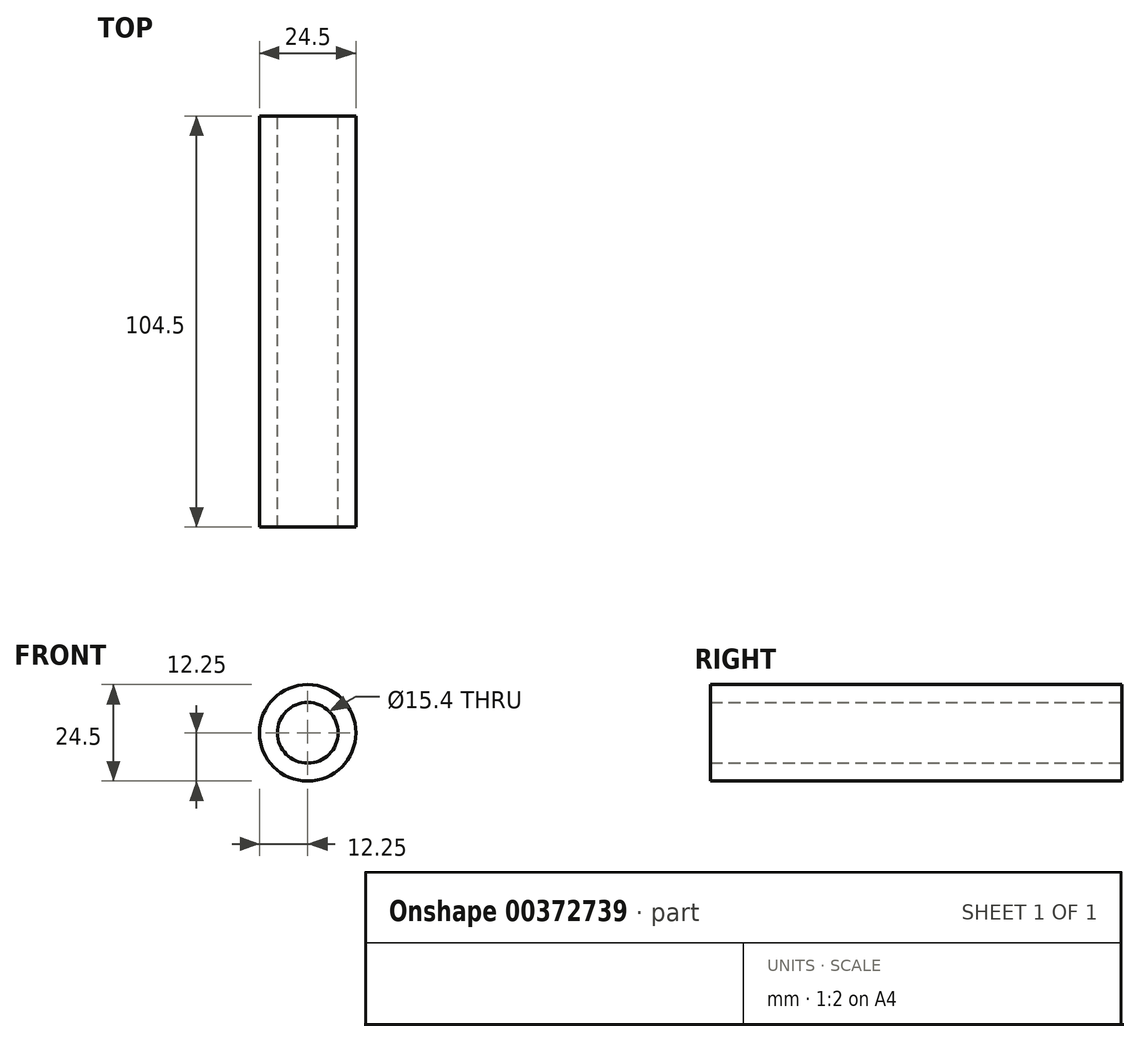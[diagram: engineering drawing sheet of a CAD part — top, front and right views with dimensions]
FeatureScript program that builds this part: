
annotation { "Feature Type Name" : "Feature", "Feature Type Description" : "" }
export const myFeature = defineFeature(function(context is Context, id is Id, definition is map)
    precondition{}
    {
        {
            var Q0;
            Q0=qCreatedBy(makeId("Front.planeOp"),FACE);
            var sketch = newSketch(context, id + "F0", { "sketchPlane" : qUnion([Q0])});
            skCircle(sketch, "E0", {"center": v(0, 0) * mm, "radius": 12.25 * mm});
            skCircle(sketch, "E1", {"center": v(0, 0) * mm, "radius": 7.7 * mm});
            skSolve(sketch);
        }
        {
            var Q0;
            Q0 = qSketchRegion(id + "F0", true);
            extrude(context, id + "F1", {"entities" : qUnion([Q0]), "depth" : 104.5 * mm});
        }
    });
